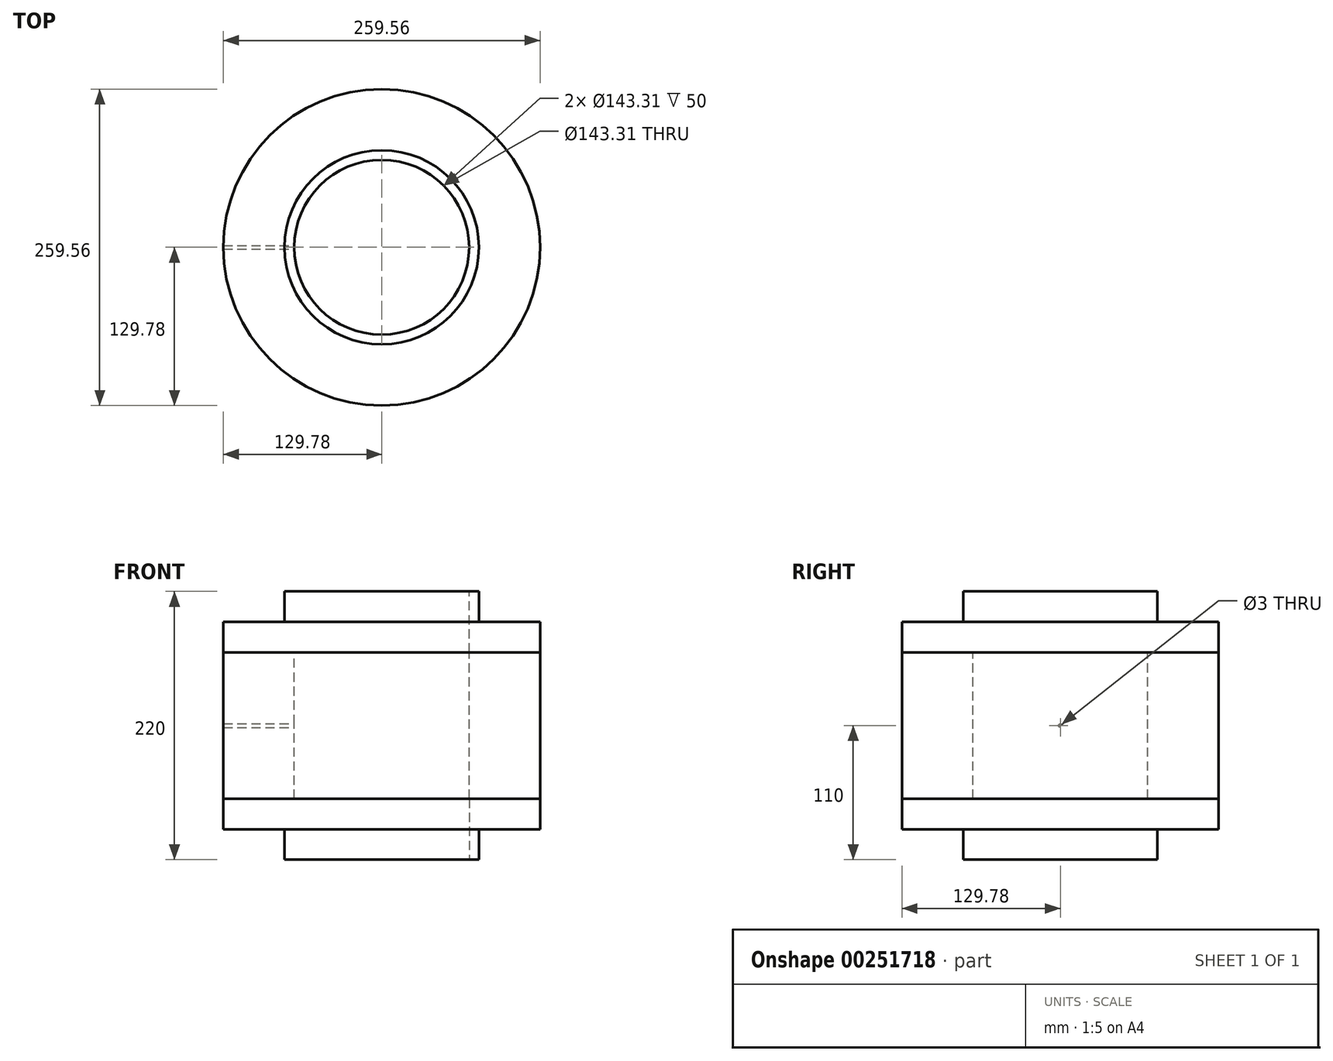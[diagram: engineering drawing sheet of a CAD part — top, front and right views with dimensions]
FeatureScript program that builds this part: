
annotation { "Feature Type Name" : "Feature", "Feature Type Description" : "" }
export const myFeature = defineFeature(function(context is Context, id is Id, definition is map)
    precondition{}
    {
        {
            var Q0;
            Q0=qCreatedBy(makeId("Top.planeOp"),FACE);
            var sketch = newSketch(context, id + "F0", { "sketchPlane" : qUnion([Q0])});
            skCircle(sketch, "E0", {"center": v(0, 0) * mm, "radius": 129.77 * mm});
            skSolve(sketch);
        }
        {
            var Q0;
            Q0 = qSketchRegion(id + "F0", true);
            extrude(context, id + "F1", {"entities" : qUnion([Q0]), "depth" : 25 * mm, "offsetDistance" : 25 * mm});
        }
        {
            var Q0;
            Q0=makeQuery(id+"F1.opExtrude","CAP_FACE",FACE,{"disambiguationData":[OSD([sQuery(id+"F0.wireOp",EDGE,"E0")])],"isStart":false});
            var sketch = newSketch(context, id + "F2", { "sketchPlane" : qUnion([Q0])});
            skCircle(sketch, "E1", {"center": v(0, 0) * mm, "radius": 79.62 * mm});
            skSolve(sketch);
        }
        {
            var Q0;
            Q0 = qSketchRegion(id + "F2", true);
            extrude(context, id + "F3", {"entities" : qUnion([Q0]), "operationType" : NewBodyOperationType.ADD, "depth" : 25 * mm, "offsetDistance" : 25 * mm});
        }
        {
            var Q0;
            Q0=makeQuery(id+"F3.opExtrude","CAP_FACE",FACE,{"disambiguationData":[OSD([sQuery(id+"F2.wireOp",EDGE,"E1")])],"isStart":false});
            var sketch = newSketch(context, id + "F4", { "sketchPlane" : qUnion([Q0])});
            skCircle(sketch, "E2", {"center": v(0, 0) * mm, "radius": 71.66 * mm});
            skSolve(sketch);
        }
        {
            var Q0;
            Q0 = qSketchRegion(id + "F4", true);
            extrude(context, id + "F5", {"entities" : qUnion([Q0]), "operationType" : NewBodyOperationType.REMOVE, "endBound" : BoundingType.UP_TO_NEXT, "oppositeDirection" : true, "depth" : 25 * mm, "offsetDistance" : 25 * mm});
        }
        {
            var Q0;
            Q0=qCreatedBy(makeId("Top.planeOp"),FACE);
            var sketch = newSketch(context, id + "F6", { "sketchPlane" : qUnion([Q0])});
            skCircle(sketch, "E3.0", {"center": v(0, 0) * mm, "radius": 129.77 * mm});
            skSolve(sketch);
        }
        {
            var Q0;
            Q0 = qSketchRegion(id + "F6", true);
            extrude(context, id + "F7", {"entities" : qUnion([Q0]), "oppositeDirection" : true, "depth" : 120 * mm, "offsetDistance" : 25 * mm});
        }
        {
            var Q0;
            Q0=qCreatedBy(makeId("Right.planeOp"),FACE);
            var sketch = newSketch(context, id + "F8", { "sketchPlane" : qUnion([Q0])});
            skLineSegment(sketch, "E4", {"start": v(129.78, 0) * mm, "end": v(129.78, -120) * mm, "construction": true});
            skPoint(sketch, "E5", {"position": v(129.78, -60) * mm});
            skCircle(sketch, "E6", {"center": v(0, -60) * mm, "radius": 1.5 * mm});
            skSolve(sketch);
        }
        {
            var Q0;
            Q0 = qSketchRegion(id + "F4", true);
            extrude(context, id + "F9", {"entities" : qUnion([Q0]), "operationType" : NewBodyOperationType.REMOVE, "endBound" : BoundingType.THROUGH_ALL, "oppositeDirection" : true, "depth" : 25 * mm, "offsetDistance" : 25 * mm});
        }
        {
            var Q0;
            Q0 = qSketchRegion(id + "F8", true);
            extrude(context, id + "F10", {"entities" : qUnion([Q0]), "operationType" : NewBodyOperationType.REMOVE, "endBound" : BoundingType.THROUGH_ALL, "oppositeDirection" : true, "depth" : 25 * mm, "offsetDistance" : 25 * mm});
        }
        {
            var Q0;
            Q0=makeQuery(id+"F7.opExtrude","CAP_FACE",FACE,{"disambiguationData":[OSD([sQuery(id+"F6.wireOp",EDGE,"E3.0")])],"isStart":true});
            var Q1;
            Q1=makeQuery(id+"F7.opExtrude","CAP_FACE",FACE,{"disambiguationData":[OSD([sQuery(id+"F6.wireOp",EDGE,"E3.0")])],"isStart":false});
            cPlane(context, id + "F11", {"entities" : qUnion([Q0, Q1]), "cplaneType" : CPlaneType.MID_PLANE, "offset" : 25 * mm, "width" : 150 * mm, "height" : 150 * mm});
        }
        {
            var Q0;
            Q0=makeQuery(id+"F1.opExtrude","SWEPT_BODY",BODY,{"disambiguationData":[OSD([sQuery(id+"F0.wireOp",EDGE,"E0")])]});
            var Q1;
            Q1=qCreatedBy(id+"F11.planeOp",FACE);
            mirror(context, id + "F12", {"entities" : qUnion([Q0]), "mirrorPlane" : qUnion([Q1])});
        }
    });
